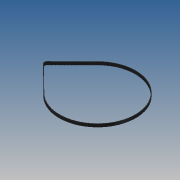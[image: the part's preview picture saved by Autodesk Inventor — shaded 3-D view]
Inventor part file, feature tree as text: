
AUTODESK INVENTOR PART (.ipt)
format: ipt  version: 2013 (Build 170138000, 138)  size: 739,328 bytes
history: native  units: mm
features: sketch x5, extrude x4, pattern_linear x1
ambient origin geometry x8: Origin, YZ Plane, XZ Plane, XY Plane, X Axis, Y Axis, Z Axis, Center Point
bodies: Solid1 (feature_tree)
feature tree (10):
  extrude  "Extrusion1"  Depth=74.802823mm
  extrude  "Extrusion2"  Depth=6.0mm TaperAngle=0.0deg
  extrude  "Extrusion4"  Depth=6.0mm TaperAngle=0.0deg
  sketch  "Sketch8"  dims[d17=6.0mm d18=0.0mm d19=2500.0mm d21=99.0mm]
  extrude  "Extrusion5"  Depth=6.0mm TaperAngle=0.0deg
  pattern_linear  "Rectangular Pattern1"  Count1=250  [1 undecoded]
  sketch  "Sketch1"  dims[d0=5.092958mm d2=74.802823mm]
  sketch  "Sketch2"  dims[d4=15.7917mm d5=6.0mm d6=0.0mm]
  sketch  "Sketch5"  dims[d7=0.375mm d8=6.0mm d9=0.0mm]
  sketch  "Sketch7"  dims[d14=0.629mm d15=6.0mm d16=0.0mm]
note: 1 required parameter value undecoded (feature->parameter linkage not recoverable at this tier; creation-order binding heuristic only, values carry confidence <= 0.55)
